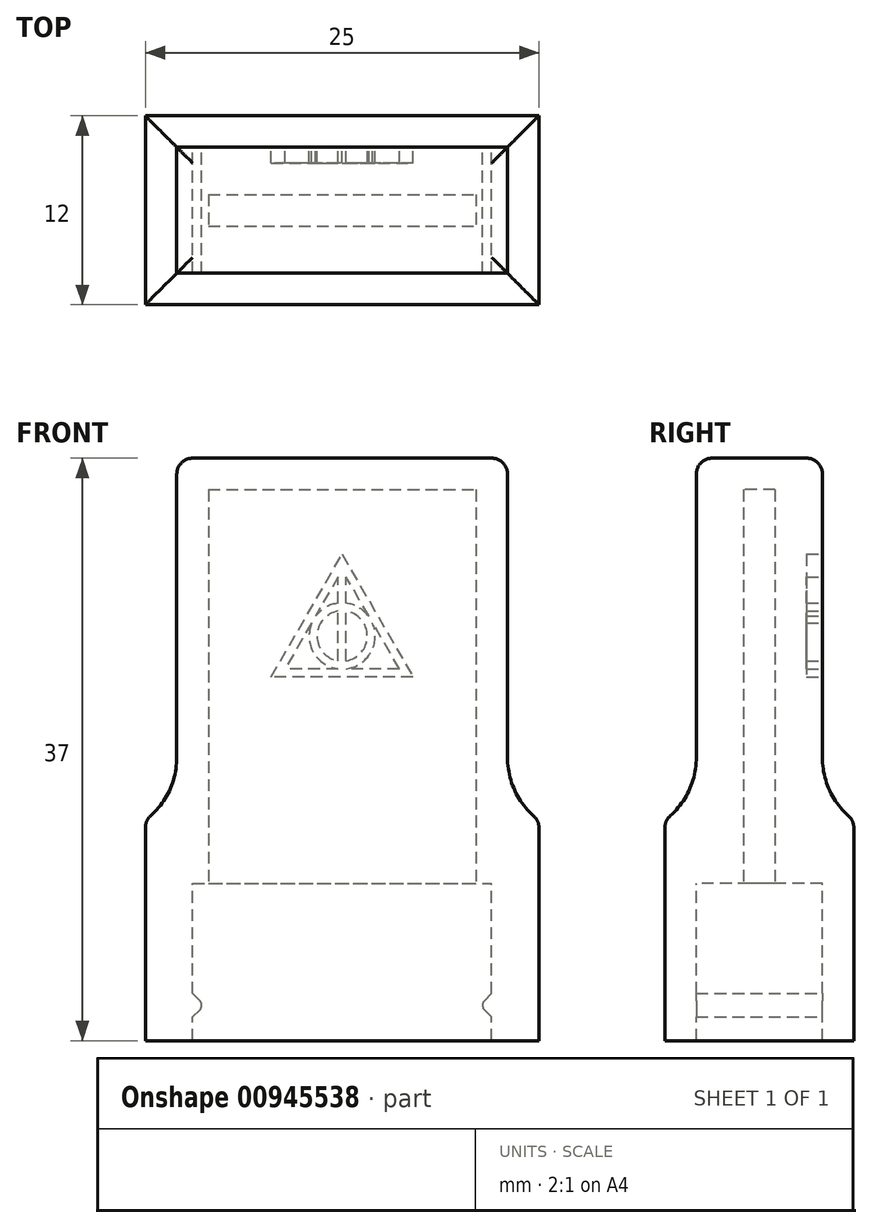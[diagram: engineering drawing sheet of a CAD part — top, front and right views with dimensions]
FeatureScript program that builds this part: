
annotation { "Feature Type Name" : "Feature", "Feature Type Description" : "" }
export const myFeature = defineFeature(function(context is Context, id is Id, definition is map)
    precondition{}
    {
        {
            var Q0;
            Q0=qCreatedBy(makeId("Top.planeOp"),FACE);
            var sketch = newSketch(context, id + "F0", { "sketchPlane" : qUnion([Q0])});
            skLineSegment(sketch, "E0.bottom", {"start": v(0, 0) * mm, "end": v(25, 0) * mm});
            skLineSegment(sketch, "E0.top", {"start": v(0, 12) * mm, "end": v(25, 12) * mm});
            skLineSegment(sketch, "E0.left", {"start": v(0, 0) * mm, "end": v(0, 12) * mm});
            skLineSegment(sketch, "E0.right", {"start": v(25, 0) * mm, "end": v(25, 12) * mm});
            skLineSegment(sketch, "E1.bottom", {"start": v(3, 10) * mm, "end": v(22, 10) * mm});
            skLineSegment(sketch, "E1.top", {"start": v(3, 2) * mm, "end": v(22, 2) * mm});
            skLineSegment(sketch, "E1.left", {"start": v(3, 10) * mm, "end": v(3, 2) * mm});
            skLineSegment(sketch, "E1.right", {"start": v(22, 10) * mm, "end": v(22, 2) * mm});
            skSolve(sketch);
        }
        {
            var Q0;
            Q0=makeQuery(id+"F0.imprint","IMPRINT",FACE,{"disambiguationData":[TD([[makeQuery(id+"F0.imprint","IMPRINT",EDGE,{"derivedFrom":sQuery(id+"F0.wireOp",EDGE,"E0.bottom")}),1.0]])]});
            extrude(context, id + "F1", {"entities" : qUnion([Q0]), "oppositeDirection" : true, "depth" : 10 * mm, "offsetDistance" : 25 * mm});
        }
        {
            var Q0;
            Q0=qCreatedBy(makeId("Top.planeOp"),FACE);
            var sketch = newSketch(context, id + "F2", { "sketchPlane" : qUnion([Q0])});
            skLineSegment(sketch, "E2.bottom", {"start": v(4, 7) * mm, "end": v(21, 7) * mm});
            skLineSegment(sketch, "E2.top", {"start": v(4, 5) * mm, "end": v(21, 5) * mm});
            skLineSegment(sketch, "E2.left", {"start": v(4, 7) * mm, "end": v(4, 5) * mm});
            skLineSegment(sketch, "E2.right", {"start": v(21, 7) * mm, "end": v(21, 5) * mm});
            skLineSegment(sketch, "E3.bottom", {"start": v(2, 10) * mm, "end": v(23, 10) * mm});
            skLineSegment(sketch, "E3.top", {"start": v(2, 2) * mm, "end": v(23, 2) * mm});
            skLineSegment(sketch, "E3.left", {"start": v(2, 10) * mm, "end": v(2, 2) * mm});
            skLineSegment(sketch, "E3.right", {"start": v(23, 10) * mm, "end": v(23, 2) * mm});
            skSolve(sketch);
        }
        {
            var Q0;
            Q0=makeQuery(id+"F2.imprint","IMPRINT",FACE,{"disambiguationData":[TD([[makeQuery(id+"F2.imprint","IMPRINT",EDGE,{"derivedFrom":sQuery(id+"F2.wireOp",EDGE,"E2.bottom")}),1.0]])]});
            extrude(context, id + "F3", {"entities" : qUnion([Q0]), "depth" : 25 * mm, "offsetDistance" : 25 * mm});
        }
        {
            var Q0;
            Q0=makeQuery(id+"F3.opExtrude","CAP_FACE",FACE,{"disambiguationData":[OSD([sQuery(id+"F2.wireOp",EDGE,"E2.bottom"),sQuery(id+"F2.wireOp",EDGE,"E2.top"),sQuery(id+"F2.wireOp",EDGE,"E2.left"),sQuery(id+"F2.wireOp",EDGE,"E2.right"),sQuery(id+"F2.wireOp",EDGE,"E3.bottom"),sQuery(id+"F2.wireOp",EDGE,"E3.top"),sQuery(id+"F2.wireOp",EDGE,"E3.left"),sQuery(id+"F2.wireOp",EDGE,"E3.right")])],"isStart":false});
            var sketch = newSketch(context, id + "F4", { "sketchPlane" : qUnion([Q0])});
            skSolve(sketch);
        }
        {
            var Q0;
            Q0=makeQuery(id+"F4.imprint","IMPRINT",FACE,{"disambiguationData":[TD([[makeQuery(id+"F4.imprint","IMPRINT",EDGE,{"derivedFrom":makeQuery(id+"F3.opExtrude","CAP_EDGE",EDGE,{"disambiguationData":[OSD([sQuery(id+"F2.wireOp",EDGE,"E2.bottom")])],"isStart":false})}),1.0]])]});
            var Q1;
            Q1=makeQuery(id+"F4.imprint","IMPRINT",FACE,{"disambiguationData":[TD([[makeQuery(id+"F4.imprint","IMPRINT",EDGE,{"derivedFrom":makeQuery(id+"F3.opExtrude","CAP_EDGE",EDGE,{"disambiguationData":[OSD([sQuery(id+"F2.wireOp",EDGE,"E2.bottom")])],"isStart":false})}),-1.0]])]});
            extrude(context, id + "F5", {"entities" : qUnion([Q0, Q1]), "operationType" : NewBodyOperationType.ADD, "depth" : 2 * mm, "offsetDistance" : 25 * mm});
        }
        {
            var Q0;
            Q0=makeQuery(id+"F1.opExtrude","CAP_FACE",FACE,{"disambiguationData":[OSD([sQuery(id+"F0.wireOp",EDGE,"E0.bottom"),sQuery(id+"F0.wireOp",EDGE,"E0.top"),sQuery(id+"F0.wireOp",EDGE,"E0.left"),sQuery(id+"F0.wireOp",EDGE,"E0.right"),sQuery(id+"F0.wireOp",EDGE,"E1.bottom"),sQuery(id+"F0.wireOp",EDGE,"E1.top"),sQuery(id+"F0.wireOp",EDGE,"E1.left"),sQuery(id+"F0.wireOp",EDGE,"E1.right")])],"isStart":true});
            var sketch = newSketch(context, id + "F6", { "sketchPlane" : qUnion([Q0])});
            skSolve(sketch);
        }
        {
            var Q0;
            Q0=makeQuery(id+"F6.imprint","IMPRINT",FACE,{"disambiguationData":[TD([[makeQuery(id+"F6.imprint","IMPRINT",EDGE,{"derivedFrom":makeQuery(id+"F1.opExtrude","CAP_EDGE",EDGE,{"disambiguationData":[OSD([sQuery(id+"F0.wireOp",EDGE,"E0.bottom")])],"isStart":true})}),1.0]])]});
            extrude(context, id + "F7", {"entities" : qUnion([Q0]), "operationType" : NewBodyOperationType.ADD, "depth" : 4 * mm, "offsetDistance" : 25 * mm});
        }
        {
            var Q0;
            Q0=qCreatedBy(makeId("Front.planeOp"),FACE);
            cPlane(context, id + "F8", {"entities" : qUnion([Q0]), "cplaneType" : CPlaneType.OFFSET, "offset" : 6 * mm, "oppositeDirection" : true, "width" : 150 * mm, "height" : 150 * mm});
        }
        {
            var Q0;
            Q0=qCreatedBy(id+"F8.planeOp",FACE);
            var sketch = newSketch(context, id + "F9", { "sketchPlane" : qUnion([Q0])});
            skLineSegment(sketch, "E4", {"start": v(0, 0) * mm, "end": v(0, -10) * mm});
            skLineSegment(sketch, "E5", {"start": v(0, -10) * mm, "end": v(3, -10) * mm});
            skLineSegment(sketch, "E6", {"start": v(3, -10) * mm, "end": v(3, -8.5) * mm});
            skLineSegment(sketch, "E7", {"start": v(3, -8.5) * mm, "end": v(3.47, -8.03) * mm});
            skLineSegment(sketch, "E8", {"start": v(3.47, -7.47) * mm, "end": v(3, -7) * mm});
            skLineSegment(sketch, "E9", {"start": v(3, -7) * mm, "end": v(3, -8.5) * mm});
            skPoint(sketch, "E10.visualSharp", {"position": v(3.75, -7.75) * mm});
            skArc(sketch, "E10.filletArc", {"start": v(3.47, -8.03) * mm, "mid": v(3.58, -7.75) * mm, "end": v(3.47, -7.47) * mm});
            skLineSegment(sketch, "E11", {"start": v(22, -8.5) * mm, "end": v(22, -7) * mm});
            skLineSegment(sketch, "E12", {"start": v(22, -7) * mm, "end": v(21.53, -7.47) * mm});
            skLineSegment(sketch, "E13", {"start": v(21.53, -8.03) * mm, "end": v(22, -8.5) * mm});
            skPoint(sketch, "E14.visualSharp", {"position": v(21.25, -7.75) * mm});
            skArc(sketch, "E14.filletArc", {"start": v(21.53, -7.47) * mm, "mid": v(21.42, -7.75) * mm, "end": v(21.53, -8.03) * mm});
            skSolve(sketch);
        }
        {
            var Q0;
            Q0=makeQuery(id+"F9.imprint","IMPRINT",FACE,{"disambiguationData":[TD([[makeQuery(id+"F9.imprint","IMPRINT",EDGE,{"derivedFrom":sQuery(id+"F9.wireOp",EDGE,"E7")}),1.0]])]});
            var Q1;
            Q1=makeQuery(id+"F9.imprint","IMPRINT",FACE,{"disambiguationData":[TD([[makeQuery(id+"F9.imprint","IMPRINT",EDGE,{"derivedFrom":sQuery(id+"F9.wireOp",EDGE,"E11")}),1.0]])]});
            extrude(context, id + "F10", {"entities" : qUnion([Q0, Q1]), "operationType" : NewBodyOperationType.ADD, "endBound" : BoundingType.UP_TO_NEXT, "depth" : 25 * mm, "offsetDistance" : 25 * mm, "hasSecondDirection" : true, "secondDirectionBound" : SecondDirectionBoundingType.UP_TO_NEXT, "secondDirectionOppositeDirection" : true, "secondDirectionDepth" : 25 * mm});
        }
        {
            var Q0;
            {var subQ0=sQuery(id+"F2.wireOp",EDGE,"E3.top");Q0=makeQuery(id+"F7.boolean.opBoolean","INTERSECT",EDGE,{"derivedFrom":[makeQuery(id+"F5.boolean.opBoolean","MERGE",FACE,{"derivedFrom":[makeQuery(id+"F3.opExtrude","SWEPT_FACE",FACE,{"disambiguationData":[OSD([subQ0])]}),makeQuery(id+"F5.opExtrude","SWEPT_FACE",FACE,{"disambiguationData":[OSD([subQ0])]})]}),makeQuery(id+"F7.opExtrude","CAP_FACE",FACE,{"disambiguationData":[OSD([sQuery(id+"F0.wireOp",EDGE,"E0.bottom"),sQuery(id+"F0.wireOp",EDGE,"E0.top"),sQuery(id+"F0.wireOp",EDGE,"E0.left"),sQuery(id+"F0.wireOp",EDGE,"E0.right"),sQuery(id+"F0.wireOp",EDGE,"E1.bottom"),sQuery(id+"F0.wireOp",EDGE,"E1.top"),sQuery(id+"F0.wireOp",EDGE,"E1.left"),sQuery(id+"F0.wireOp",EDGE,"E1.right")])],"isStart":false})]});}
            var Q1;
            {var subQ0=sQuery(id+"F2.wireOp",EDGE,"E3.right");Q1=makeQuery(id+"F7.boolean.opBoolean","INTERSECT",EDGE,{"derivedFrom":[makeQuery(id+"F5.boolean.opBoolean","MERGE",FACE,{"derivedFrom":[makeQuery(id+"F3.opExtrude","SWEPT_FACE",FACE,{"disambiguationData":[OSD([subQ0])]}),makeQuery(id+"F5.opExtrude","SWEPT_FACE",FACE,{"disambiguationData":[OSD([subQ0])]})]}),makeQuery(id+"F7.opExtrude","CAP_FACE",FACE,{"disambiguationData":[OSD([sQuery(id+"F0.wireOp",EDGE,"E0.bottom"),sQuery(id+"F0.wireOp",EDGE,"E0.top"),sQuery(id+"F0.wireOp",EDGE,"E0.left"),sQuery(id+"F0.wireOp",EDGE,"E0.right"),sQuery(id+"F0.wireOp",EDGE,"E1.bottom"),sQuery(id+"F0.wireOp",EDGE,"E1.top"),sQuery(id+"F0.wireOp",EDGE,"E1.left"),sQuery(id+"F0.wireOp",EDGE,"E1.right")])],"isStart":false})]});}
            var Q2;
            {var subQ0=sQuery(id+"F2.wireOp",EDGE,"E3.bottom");Q2=makeQuery(id+"F7.boolean.opBoolean","INTERSECT",EDGE,{"derivedFrom":[makeQuery(id+"F5.boolean.opBoolean","MERGE",FACE,{"derivedFrom":[makeQuery(id+"F3.opExtrude","SWEPT_FACE",FACE,{"disambiguationData":[OSD([subQ0])]}),makeQuery(id+"F5.opExtrude","SWEPT_FACE",FACE,{"disambiguationData":[OSD([subQ0])]})]}),makeQuery(id+"F7.opExtrude","CAP_FACE",FACE,{"disambiguationData":[OSD([sQuery(id+"F0.wireOp",EDGE,"E0.bottom"),sQuery(id+"F0.wireOp",EDGE,"E0.top"),sQuery(id+"F0.wireOp",EDGE,"E0.left"),sQuery(id+"F0.wireOp",EDGE,"E0.right"),sQuery(id+"F0.wireOp",EDGE,"E1.bottom"),sQuery(id+"F0.wireOp",EDGE,"E1.top"),sQuery(id+"F0.wireOp",EDGE,"E1.left"),sQuery(id+"F0.wireOp",EDGE,"E1.right")])],"isStart":false})]});}
            var Q3;
            {var subQ0=sQuery(id+"F2.wireOp",EDGE,"E3.left");Q3=makeQuery(id+"F7.boolean.opBoolean","INTERSECT",EDGE,{"derivedFrom":[makeQuery(id+"F5.boolean.opBoolean","MERGE",FACE,{"derivedFrom":[makeQuery(id+"F3.opExtrude","SWEPT_FACE",FACE,{"disambiguationData":[OSD([subQ0])]}),makeQuery(id+"F5.opExtrude","SWEPT_FACE",FACE,{"disambiguationData":[OSD([subQ0])]})]}),makeQuery(id+"F7.opExtrude","CAP_FACE",FACE,{"disambiguationData":[OSD([sQuery(id+"F0.wireOp",EDGE,"E0.bottom"),sQuery(id+"F0.wireOp",EDGE,"E0.top"),sQuery(id+"F0.wireOp",EDGE,"E0.left"),sQuery(id+"F0.wireOp",EDGE,"E0.right"),sQuery(id+"F0.wireOp",EDGE,"E1.bottom"),sQuery(id+"F0.wireOp",EDGE,"E1.top"),sQuery(id+"F0.wireOp",EDGE,"E1.left"),sQuery(id+"F0.wireOp",EDGE,"E1.right")])],"isStart":false})]});}
            fillet(context, id + "F11", {"entities" : qUnion([Q0, Q1, Q2, Q3]), "radius" : 5 * mm, "tangentPropagation" : true, "allowEdgeOverflow" : false});
        }
        {
            var Q0;
            Q0=makeQuery(id+"F5.opExtrude","CAP_EDGE",EDGE,{"disambiguationData":[OSD([sQuery(id+"F2.wireOp",EDGE,"E3.right")])],"isStart":false});
            var Q1;
            Q1=makeQuery(id+"F5.opExtrude","CAP_EDGE",EDGE,{"disambiguationData":[OSD([sQuery(id+"F2.wireOp",EDGE,"E3.top")])],"isStart":false});
            var Q2;
            Q2=makeQuery(id+"F5.opExtrude","CAP_EDGE",EDGE,{"disambiguationData":[OSD([sQuery(id+"F2.wireOp",EDGE,"E3.left")])],"isStart":false});
            var Q3;
            Q3=makeQuery(id+"F5.opExtrude","CAP_EDGE",EDGE,{"disambiguationData":[OSD([sQuery(id+"F2.wireOp",EDGE,"E3.bottom")])],"isStart":false});
            var Q4;
            {var subQ0=sQuery(id+"F0.wireOp",EDGE,"E0.top");var subQ1=sQuery(id+"F2.wireOp",EDGE,"E3.bottom");Q4=makeQuery(id+"F11.opFillet","BLEND_EDGE",EDGE,{"blendedFrom":[makeQuery(id+"F7.boolean.opBoolean","INTERSECT",EDGE,{"derivedFrom":[makeQuery(id+"F5.boolean.opBoolean","MERGE",FACE,{"derivedFrom":[makeQuery(id+"F3.opExtrude","SWEPT_FACE",FACE,{"disambiguationData":[OSD([subQ1])]}),makeQuery(id+"F5.opExtrude","SWEPT_FACE",FACE,{"disambiguationData":[OSD([subQ1])]})]}),makeQuery(id+"F7.opExtrude","CAP_FACE",FACE,{"disambiguationData":[OSD([sQuery(id+"F0.wireOp",EDGE,"E0.bottom"),subQ0,sQuery(id+"F0.wireOp",EDGE,"E0.left"),sQuery(id+"F0.wireOp",EDGE,"E0.right"),sQuery(id+"F0.wireOp",EDGE,"E1.bottom"),sQuery(id+"F0.wireOp",EDGE,"E1.top"),sQuery(id+"F0.wireOp",EDGE,"E1.left"),sQuery(id+"F0.wireOp",EDGE,"E1.right")])],"isStart":false})]}),makeQuery(id+"F7.boolean.opBoolean","MERGE",FACE,{"derivedFrom":[makeQuery(id+"F1.opExtrude","SWEPT_FACE",FACE,{"disambiguationData":[OSD([subQ0])]}),makeQuery(id+"F7.opExtrude","SWEPT_FACE",FACE,{"disambiguationData":[OSD([subQ0])]})]})],"blendedInto":[makeQuery(id+"F7.boolean.opBoolean","MERGE",FACE,{"derivedFrom":[makeQuery(id+"F1.opExtrude","SWEPT_FACE",FACE,{"disambiguationData":[OSD([subQ0])]}),makeQuery(id+"F7.opExtrude","SWEPT_FACE",FACE,{"disambiguationData":[OSD([subQ0])]})]})]});}
            var Q5;
            {var subQ0=sQuery(id+"F0.wireOp",EDGE,"E0.right");var subQ1=sQuery(id+"F2.wireOp",EDGE,"E3.right");Q5=makeQuery(id+"F11.opFillet","BLEND_EDGE",EDGE,{"blendedFrom":[makeQuery(id+"F7.boolean.opBoolean","INTERSECT",EDGE,{"derivedFrom":[makeQuery(id+"F5.boolean.opBoolean","MERGE",FACE,{"derivedFrom":[makeQuery(id+"F3.opExtrude","SWEPT_FACE",FACE,{"disambiguationData":[OSD([subQ1])]}),makeQuery(id+"F5.opExtrude","SWEPT_FACE",FACE,{"disambiguationData":[OSD([subQ1])]})]}),makeQuery(id+"F7.opExtrude","CAP_FACE",FACE,{"disambiguationData":[OSD([sQuery(id+"F0.wireOp",EDGE,"E0.bottom"),sQuery(id+"F0.wireOp",EDGE,"E0.top"),sQuery(id+"F0.wireOp",EDGE,"E0.left"),subQ0,sQuery(id+"F0.wireOp",EDGE,"E1.bottom"),sQuery(id+"F0.wireOp",EDGE,"E1.top"),sQuery(id+"F0.wireOp",EDGE,"E1.left"),sQuery(id+"F0.wireOp",EDGE,"E1.right")])],"isStart":false})]}),makeQuery(id+"F7.boolean.opBoolean","MERGE",FACE,{"derivedFrom":[makeQuery(id+"F1.opExtrude","SWEPT_FACE",FACE,{"disambiguationData":[OSD([subQ0])]}),makeQuery(id+"F7.opExtrude","SWEPT_FACE",FACE,{"disambiguationData":[OSD([subQ0])]})]})],"blendedInto":[makeQuery(id+"F7.boolean.opBoolean","MERGE",FACE,{"derivedFrom":[makeQuery(id+"F1.opExtrude","SWEPT_FACE",FACE,{"disambiguationData":[OSD([subQ0])]}),makeQuery(id+"F7.opExtrude","SWEPT_FACE",FACE,{"disambiguationData":[OSD([subQ0])]})]})]});}
            var Q6;
            {var subQ0=sQuery(id+"F0.wireOp",EDGE,"E0.bottom");var subQ1=sQuery(id+"F2.wireOp",EDGE,"E3.top");Q6=makeQuery(id+"F11.opFillet","BLEND_EDGE",EDGE,{"blendedFrom":[makeQuery(id+"F7.boolean.opBoolean","INTERSECT",EDGE,{"derivedFrom":[makeQuery(id+"F5.boolean.opBoolean","MERGE",FACE,{"derivedFrom":[makeQuery(id+"F3.opExtrude","SWEPT_FACE",FACE,{"disambiguationData":[OSD([subQ1])]}),makeQuery(id+"F5.opExtrude","SWEPT_FACE",FACE,{"disambiguationData":[OSD([subQ1])]})]}),makeQuery(id+"F7.opExtrude","CAP_FACE",FACE,{"disambiguationData":[OSD([subQ0,sQuery(id+"F0.wireOp",EDGE,"E0.top"),sQuery(id+"F0.wireOp",EDGE,"E0.left"),sQuery(id+"F0.wireOp",EDGE,"E0.right"),sQuery(id+"F0.wireOp",EDGE,"E1.bottom"),sQuery(id+"F0.wireOp",EDGE,"E1.top"),sQuery(id+"F0.wireOp",EDGE,"E1.left"),sQuery(id+"F0.wireOp",EDGE,"E1.right")])],"isStart":false})]}),makeQuery(id+"F7.boolean.opBoolean","MERGE",FACE,{"derivedFrom":[makeQuery(id+"F1.opExtrude","SWEPT_FACE",FACE,{"disambiguationData":[OSD([subQ0])]}),makeQuery(id+"F7.opExtrude","SWEPT_FACE",FACE,{"disambiguationData":[OSD([subQ0])]})]})],"blendedInto":[makeQuery(id+"F7.boolean.opBoolean","MERGE",FACE,{"derivedFrom":[makeQuery(id+"F1.opExtrude","SWEPT_FACE",FACE,{"disambiguationData":[OSD([subQ0])]}),makeQuery(id+"F7.opExtrude","SWEPT_FACE",FACE,{"disambiguationData":[OSD([subQ0])]})]})]});}
            var Q7;
            {var subQ0=sQuery(id+"F0.wireOp",EDGE,"E0.left");var subQ1=sQuery(id+"F2.wireOp",EDGE,"E3.left");Q7=makeQuery(id+"F11.opFillet","BLEND_EDGE",EDGE,{"blendedFrom":[makeQuery(id+"F7.boolean.opBoolean","INTERSECT",EDGE,{"derivedFrom":[makeQuery(id+"F5.boolean.opBoolean","MERGE",FACE,{"derivedFrom":[makeQuery(id+"F3.opExtrude","SWEPT_FACE",FACE,{"disambiguationData":[OSD([subQ1])]}),makeQuery(id+"F5.opExtrude","SWEPT_FACE",FACE,{"disambiguationData":[OSD([subQ1])]})]}),makeQuery(id+"F7.opExtrude","CAP_FACE",FACE,{"disambiguationData":[OSD([sQuery(id+"F0.wireOp",EDGE,"E0.bottom"),sQuery(id+"F0.wireOp",EDGE,"E0.top"),subQ0,sQuery(id+"F0.wireOp",EDGE,"E0.right"),sQuery(id+"F0.wireOp",EDGE,"E1.bottom"),sQuery(id+"F0.wireOp",EDGE,"E1.top"),sQuery(id+"F0.wireOp",EDGE,"E1.left"),sQuery(id+"F0.wireOp",EDGE,"E1.right")])],"isStart":false})]}),makeQuery(id+"F7.boolean.opBoolean","MERGE",FACE,{"derivedFrom":[makeQuery(id+"F1.opExtrude","SWEPT_FACE",FACE,{"disambiguationData":[OSD([subQ0])]}),makeQuery(id+"F7.opExtrude","SWEPT_FACE",FACE,{"disambiguationData":[OSD([subQ0])]})]})],"blendedInto":[makeQuery(id+"F7.boolean.opBoolean","MERGE",FACE,{"derivedFrom":[makeQuery(id+"F1.opExtrude","SWEPT_FACE",FACE,{"disambiguationData":[OSD([subQ0])]}),makeQuery(id+"F7.opExtrude","SWEPT_FACE",FACE,{"disambiguationData":[OSD([subQ0])]})]})]});}
            fillet(context, id + "F12", {"entities" : qUnion([Q0, Q1, Q2, Q3, Q4, Q5, Q6, Q7]), "radius" : 1 * mm, "tangentPropagation" : true, "allowEdgeOverflow" : false});
        }
        {
            var Q0;
            {var subQ0=sQuery(id+"F2.wireOp",EDGE,"E3.bottom");Q0=makeQuery(id+"F5.boolean.opBoolean","MERGE",FACE,{"derivedFrom":[makeQuery(id+"F3.opExtrude","SWEPT_FACE",FACE,{"disambiguationData":[OSD([subQ0])]}),makeQuery(id+"F5.opExtrude","SWEPT_FACE",FACE,{"disambiguationData":[OSD([subQ0])]})]});}
            var sketch = newSketch(context, id + "F13", { "sketchPlane" : qUnion([Q0])});
            skLineSegment(sketch, "E15", {"start": v(-17, 13.1) * mm, "end": v(-8, 13.1) * mm});
            skLineSegment(sketch, "E16", {"start": v(-8, 13.1) * mm, "end": v(-12.5, 20.9) * mm});
            skLineSegment(sketch, "E17", {"start": v(-12.5, 20.9) * mm, "end": v(-17, 13.1) * mm});
            skLineSegment(sketch, "E18", {"start": v(-16.13, 13.6) * mm, "end": v(-14.44, 16.54) * mm});
            skLineSegment(sketch, "E19", {"start": v(-12.25, 19.47) * mm, "end": v(-10.8, 16.97) * mm});
            skLineSegment(sketch, "E20", {"start": v(-16.13, 13.6) * mm, "end": v(-12.75, 13.6) * mm});
            skLineSegment(sketch, "E21", {"start": v(-12.75, 13.6) * mm, "end": v(-12.75, 13.62) * mm});
            skLineSegment(sketch, "E22", {"start": v(-12.25, 13.6) * mm, "end": v(-12.25, 13.62) * mm});
            skArc(sketch, "E23", {"start": v(-12.75, 17.79) * mm, "mid": v(-13.55, 17.52) * mm, "end": v(-14.18, 16.96) * mm});
            skPoint(sketch, "E23.first.point", {"position": v(-14.32, 16.75) * mm});
            skPoint(sketch, "E23.second.point", {"position": v(-12.5, 13.6) * mm});
            skPoint(sketch, "E23.third.point", {"position": v(-10.68, 16.75) * mm});
            skArc(sketch, "E24", {"start": v(-12.75, 17.28) * mm, "mid": v(-14.1, 15.7) * mm, "end": v(-12.75, 14.13) * mm});
            skPoint(sketch, "E25.orphan", {"position": v(-12.5, 19.9) * mm});
            skLineSegment(sketch, "E26.trimOffspring", {"start": v(-12.25, 17.79) * mm, "end": v(-12.25, 19.47) * mm});
            skLineSegment(sketch, "E27.trimOffspring", {"start": v(-12.75, 17.79) * mm, "end": v(-12.75, 19.47) * mm});
            skArc(sketch, "E28.trimOffspring", {"start": v(-12.25, 14.13) * mm, "mid": v(-10.9, 15.7) * mm, "end": v(-12.25, 17.28) * mm});
            skLineSegment(sketch, "E29.trimOffspring", {"start": v(-12.75, 14.13) * mm, "end": v(-12.75, 17.28) * mm});
            skLineSegment(sketch, "E30.trimOffspring", {"start": v(-12.25, 14.13) * mm, "end": v(-12.25, 17.28) * mm});
            skArc(sketch, "E31.trimOffspring", {"start": v(-12.25, 13.62) * mm, "mid": v(-10.68, 14.65) * mm, "end": v(-10.57, 16.53) * mm});
            skLineSegment(sketch, "E32.trimOffspring", {"start": v(-12.25, 13.6) * mm, "end": v(-8.87, 13.6) * mm});
            skLineSegment(sketch, "E33", {"start": v(-14.2, 16.97) * mm, "end": v(-14.17, 16.96) * mm});
            skLineSegment(sketch, "E34.trimOffspring", {"start": v(-14.2, 16.97) * mm, "end": v(-12.75, 19.47) * mm});
            skArc(sketch, "E35.trimOffspring", {"start": v(-14.43, 16.53) * mm, "mid": v(-14.32, 14.65) * mm, "end": v(-12.75, 13.62) * mm});
            skLineSegment(sketch, "E36", {"start": v(-14.44, 16.54) * mm, "end": v(-14.39, 16.5) * mm});
            skLineSegment(sketch, "E37", {"start": v(-10.8, 16.97) * mm, "end": v(-11.02, 16.84) * mm});
            skLineSegment(sketch, "E38", {"start": v(-10.56, 16.54) * mm, "end": v(-10.66, 16.48) * mm});
            skLineSegment(sketch, "E39.trimOffspring", {"start": v(-10.56, 16.54) * mm, "end": v(-8.87, 13.6) * mm});
            skArc(sketch, "E40.trimOffspring", {"start": v(-10.82, 16.96) * mm, "mid": v(-11.45, 17.52) * mm, "end": v(-12.25, 17.79) * mm});
            skSolve(sketch);
        }
        {
            var Q0;
            Q0=makeQuery(id+"F13.imprint","IMPRINT",FACE,{"disambiguationData":[TD([[makeQuery(id+"F13.imprint","IMPRINT",EDGE,{"derivedFrom":sQuery(id+"F13.wireOp",EDGE,"E15")}),1.0]])]});
            extrude(context, id + "F14", {"entities" : qUnion([Q0]), "operationType" : NewBodyOperationType.REMOVE, "oppositeDirection" : true, "depth" : 1 * mm, "offsetDistance" : 25 * mm});
        }
    });
